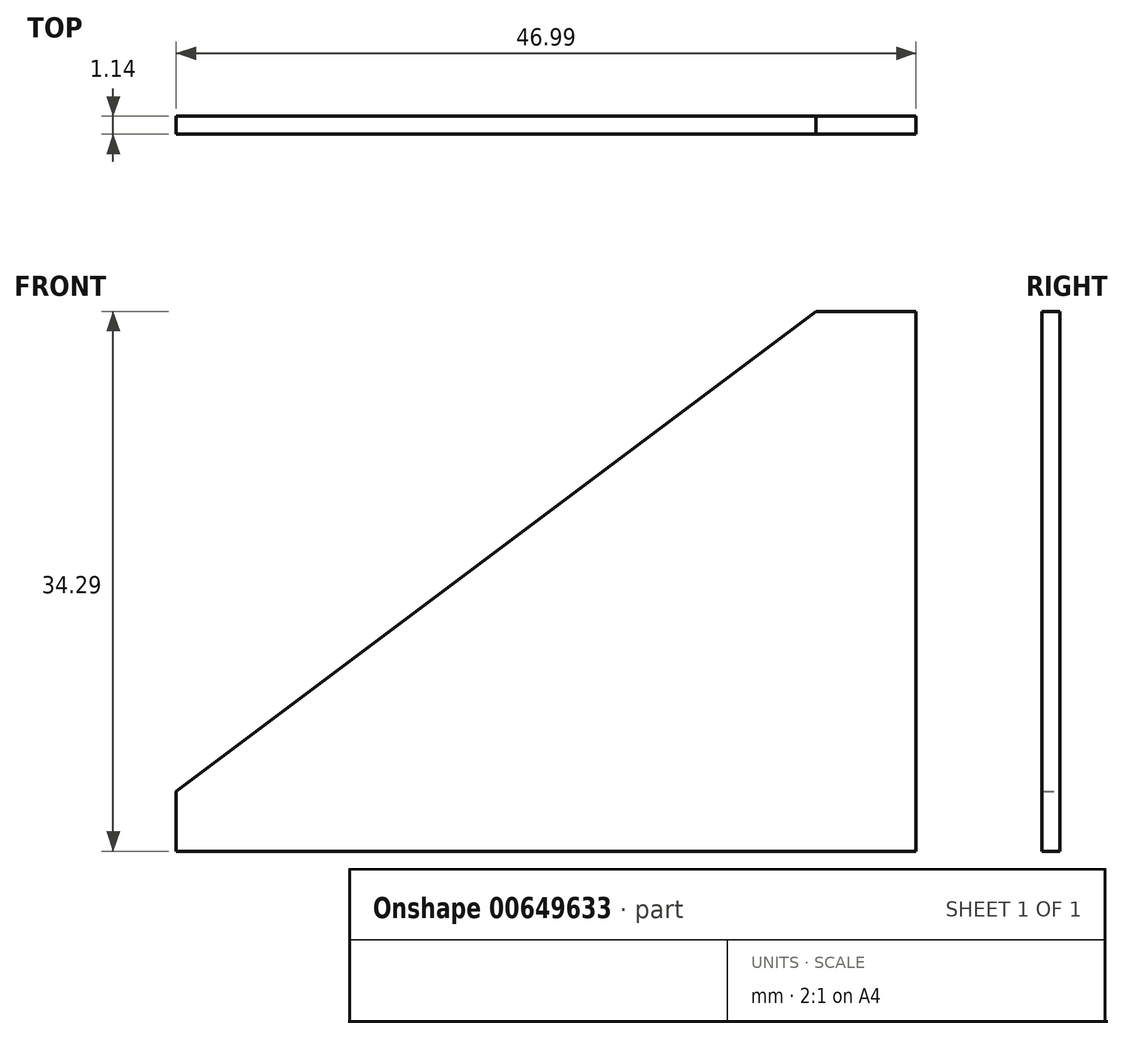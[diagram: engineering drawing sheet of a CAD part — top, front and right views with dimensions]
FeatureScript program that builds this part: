
annotation { "Feature Type Name" : "Feature", "Feature Type Description" : "" }
export const myFeature = defineFeature(function(context is Context, id is Id, definition is map)
    precondition{}
    {
        {
            var Q0;
            Q0=qCreatedBy(makeId("Front.planeOp"),FACE);
            var sketch = newSketch(context, id + "F0", { "sketchPlane" : qUnion([Q0])});
            skLineSegment(sketch, "E0", {"start": v(0, 0) * mm, "end": v(0, 34.3) * mm});
            skLineSegment(sketch, "E1", {"start": v(0, 34.3) * mm, "end": v(-6.35, 34.3) * mm});
            skLineSegment(sketch, "E2", {"start": v(-6.35, 34.3) * mm, "end": v(-47, 3.8) * mm});
            skLineSegment(sketch, "E3", {"start": v(-47, 3.81) * mm, "end": v(-47, 0) * mm});
            skLineSegment(sketch, "E4", {"start": v(-47, 0) * mm, "end": v(0, 0) * mm});
            skSolve(sketch);
        }
        {
            var Q0;
            Q0=makeQuery(id+"F0.imprint","IMPRINT",FACE,{"disambiguationData":[TD([[makeQuery(id+"F0.imprint","IMPRINT",EDGE,{"derivedFrom":sQuery(id+"F0.wireOp",EDGE,"E0")}),1.0]])]});
            extrude(context, id + "F1", {"entities" : qUnion([Q0]), "depth" : 1.14 * mm, "offsetDistance" : 25.4 * mm});
        }
    });
